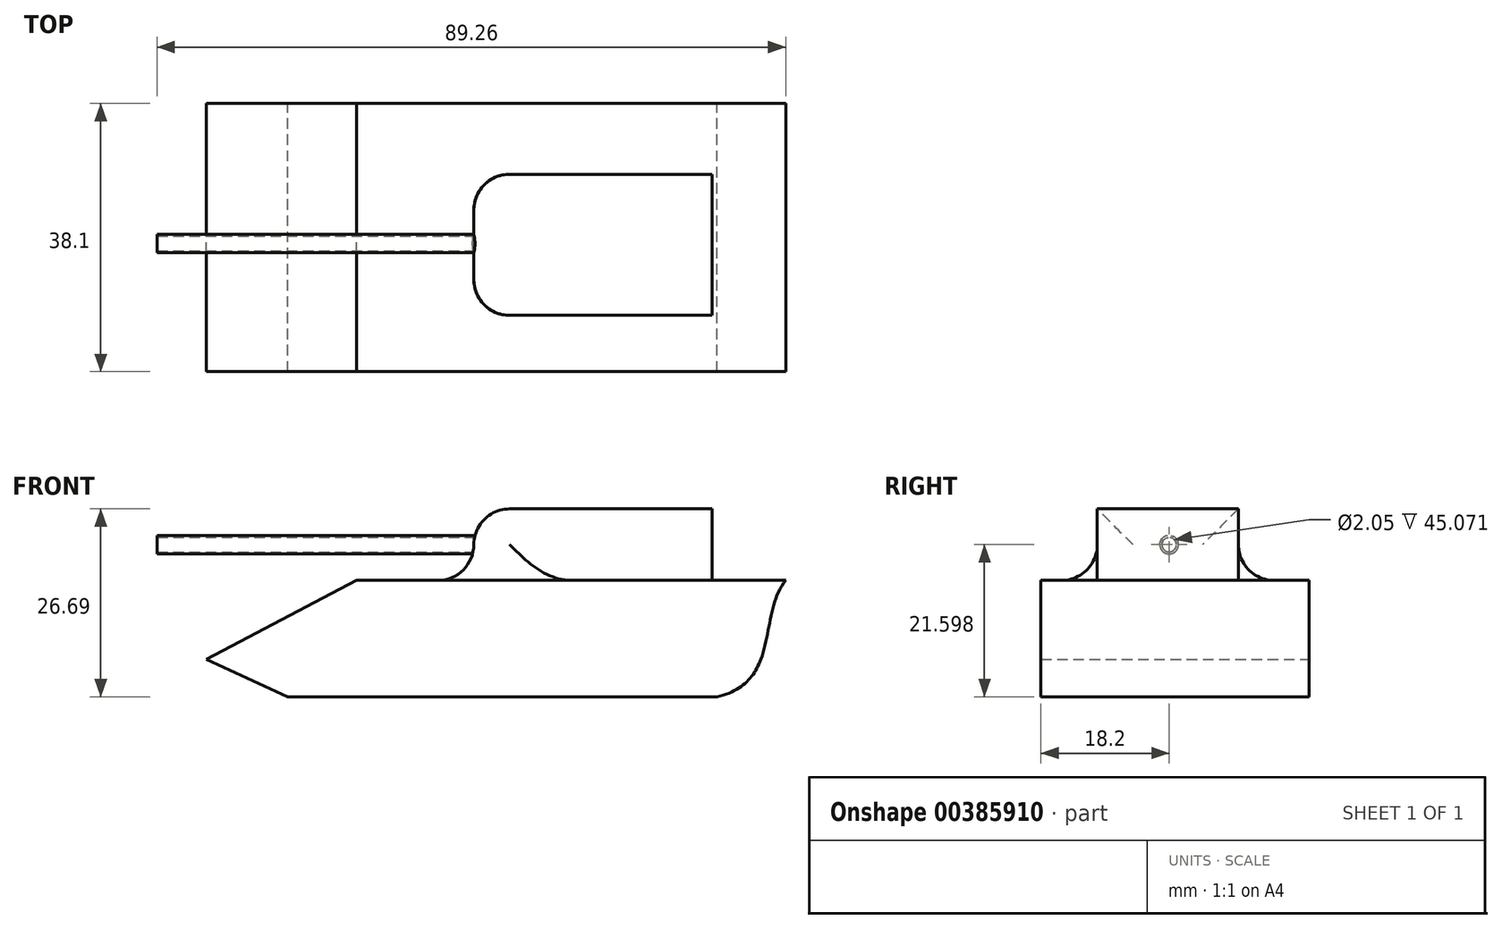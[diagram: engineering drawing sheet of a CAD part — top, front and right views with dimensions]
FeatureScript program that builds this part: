
annotation { "Feature Type Name" : "Feature", "Feature Type Description" : "" }
export const myFeature = defineFeature(function(context is Context, id is Id, definition is map)
    precondition{}
    {
        {
            var Q0;
            Q0=qCreatedBy(makeId("Front.planeOp"),FACE);
            var sketch = newSketch(context, id + "F0", { "sketchPlane" : qUnion([Q0])});
            skLineSegment(sketch, "E0", {"start": v(-53.95, -11.24) * mm, "end": v(-32.66, 0) * mm});
            skLineSegment(sketch, "E1", {"start": v(-53.95, -11.24) * mm, "end": v(-42.45, -16.53) * mm});
            skLineSegment(sketch, "E2", {"start": v(-32.66, 0) * mm, "end": v(28.3, 0) * mm});
            skLineSegment(sketch, "E3", {"start": v(-42.45, -16.53) * mm, "end": v(18.51, -16.53) * mm});
            skFitSpline(sketch, "E4", {"points": [v(18.51, -16.53) * mm, v(28.3, 0) * mm], "startDerivative": vector(27.34, 5.8) * mm, "endDerivative": vector(11.8, 14.07) * mm});
            skLineSegment(sketch, "E5", {"start": v(-53.95, -11.24) * mm, "end": v(24.76, -11.24) * mm});
            skSolve(sketch);
        }
        {
            var Q0;
            Q0 = qSketchRegion(id + "F0", true);
            var Q1;
            Q1 = qSketchRegion(id + "F2", true);
            extrude(context, id + "F1", {"entities" : qUnion([Q0, Q1]), "depth" : 38.1 * mm});
        }
        {
            var Q0;
            Q0=qCreatedBy(makeId("Top.planeOp"),FACE);
            var sketch = newSketch(context, id + "F2", { "sketchPlane" : qUnion([Q0])});
            skLineSegment(sketch, "E6", {"start": v(-16, -10.06) * mm, "end": v(17.82, -10.06) * mm});
            skLineSegment(sketch, "E7", {"start": v(17.82, -10.06) * mm, "end": v(17.82, -30.1) * mm});
            skLineSegment(sketch, "E8", {"start": v(17.82, -30.1) * mm, "end": v(-16, -30.1) * mm});
            skLineSegment(sketch, "E9", {"start": v(-16, -10.06) * mm, "end": v(-16, -30.1) * mm});
            skSolve(sketch);
        }
        {
            var Q0;
            Q0 = qSketchRegion(id + "F2", true);
            extrude(context, id + "F3", {"entities" : qUnion([Q0]), "operationType" : NewBodyOperationType.ADD, "depth" : 10.16 * mm});
        }
        {
            var Q0;
            Q0=makeQuery(id+"F3.opExtrude","SWEPT_FACE",FACE,{"disambiguationData":[OSD([sQuery(id+"F2.wireOp",EDGE,"E9")])]});
            fillet(context, id + "F4", {"entities" : qUnion([Q0]), "radius" : 5.08 * mm, "tangentPropagation" : true, "allowEdgeOverflow" : false});
        }
        {
            var Q0;
            Q0=qCreatedBy(makeId("Right.planeOp"),FACE);
            var sketch = newSketch(context, id + "F5", { "sketchPlane" : qUnion([Q0])});
            skCircle(sketch, "E10", {"center": v(-19.9, 5.07) * mm, "radius": 1.32 * mm});
            skCircle(sketch, "E11", {"center": v(-19.9, 5.07) * mm, "radius": 1.02 * mm});
            skSolve(sketch);
        }
        {
            var Q0;
            Q0 = qSketchRegion(id + "F5", true);
            extrude(context, id + "F6", {"entities" : qUnion([Q0]), "operationType" : NewBodyOperationType.ADD, "oppositeDirection" : true, "depth" : 60.96 * mm});
        }
    });
